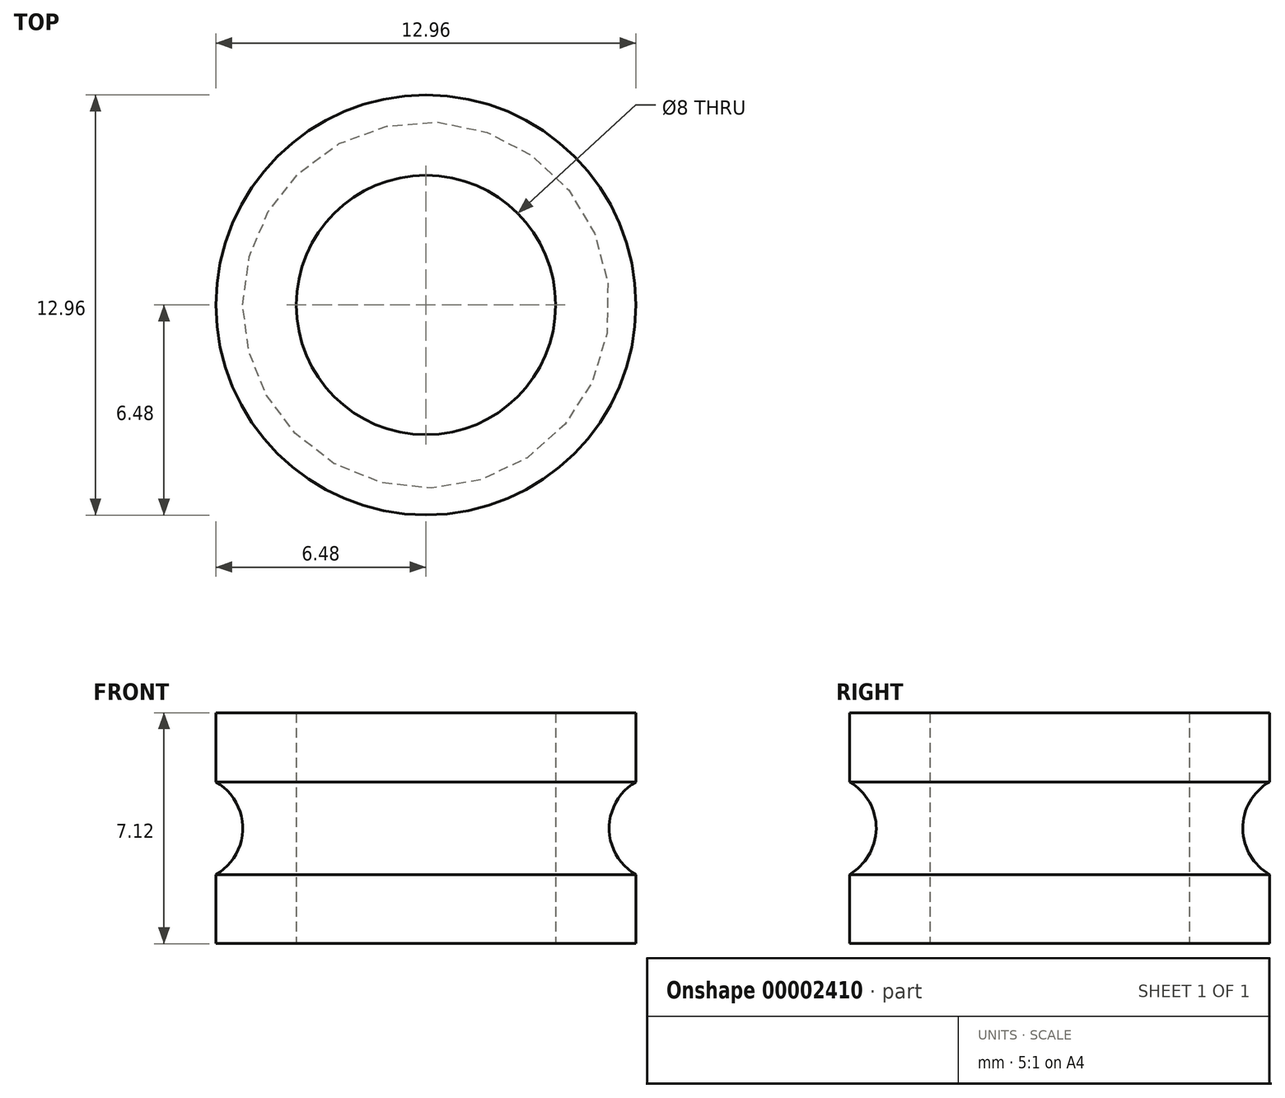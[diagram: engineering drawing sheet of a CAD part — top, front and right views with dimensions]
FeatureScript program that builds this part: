
annotation { "Feature Type Name" : "Feature", "Feature Type Description" : "" }
export const myFeature = defineFeature(function(context is Context, id is Id, definition is map)
    precondition{}
    {
        {
            var Q0;
            Q0=qCreatedBy(makeId("Top.planeOp"),FACE);
            var sketch = newSketch(context, id + "F0", { "sketchPlane" : qUnion([Q0])});
            skCircle(sketch, "E0", {"center": v(0, 0) * mm, "radius": 4 * mm});
            skCircle(sketch, "E1", {"center": v(0, 0) * mm, "radius": 6.48 * mm});
            skSolve(sketch);
        }
        {
            var Q0;
            Q0=qSketchRegion(id+"F0",true);
            extrude(context, id + "F1", {"entities" : qUnion([Q0]), "endBound" : BoundingType.SYMMETRIC, "depth" : 7.11 * mm});
        }
        {
            var Q0;
            Q0=qCreatedBy(makeId("Front.planeOp"),FACE);
            var sketch = newSketch(context, id + "F2", { "sketchPlane" : qUnion([Q0])});
            skCircle(sketch, "E2", {"center": v(7.3, 0) * mm, "radius": 1.65 * mm});
            skLineSegment(sketch, "E3", {"start": v(0, 0) * mm, "end": v(0, -4.56) * mm, "construction": true});
            skSolve(sketch);
        }
        {
            var Q0;
            Q0=makeQuery(id+"F2.imprint","IMPRINT",FACE,{"disambiguationData":[TD([[makeQuery(id+"F2.imprint","IMPRINT",EDGE,{"derivedFrom":sQuery(id+"F2.wireOp",EDGE,"E2")}),1.0]])]});
            var Q1;
            Q1=sQuery(id+"F2.wireOp",EDGE,"E3");
            revolve(context, id + "F3", {"operationType" : NewBodyOperationType.REMOVE, "entities" : qUnion([Q0]), "axis" : qUnion([Q1]), "revolveType" : RevolveType.FULL, "oppositeDirection" : true});
        }
    });
